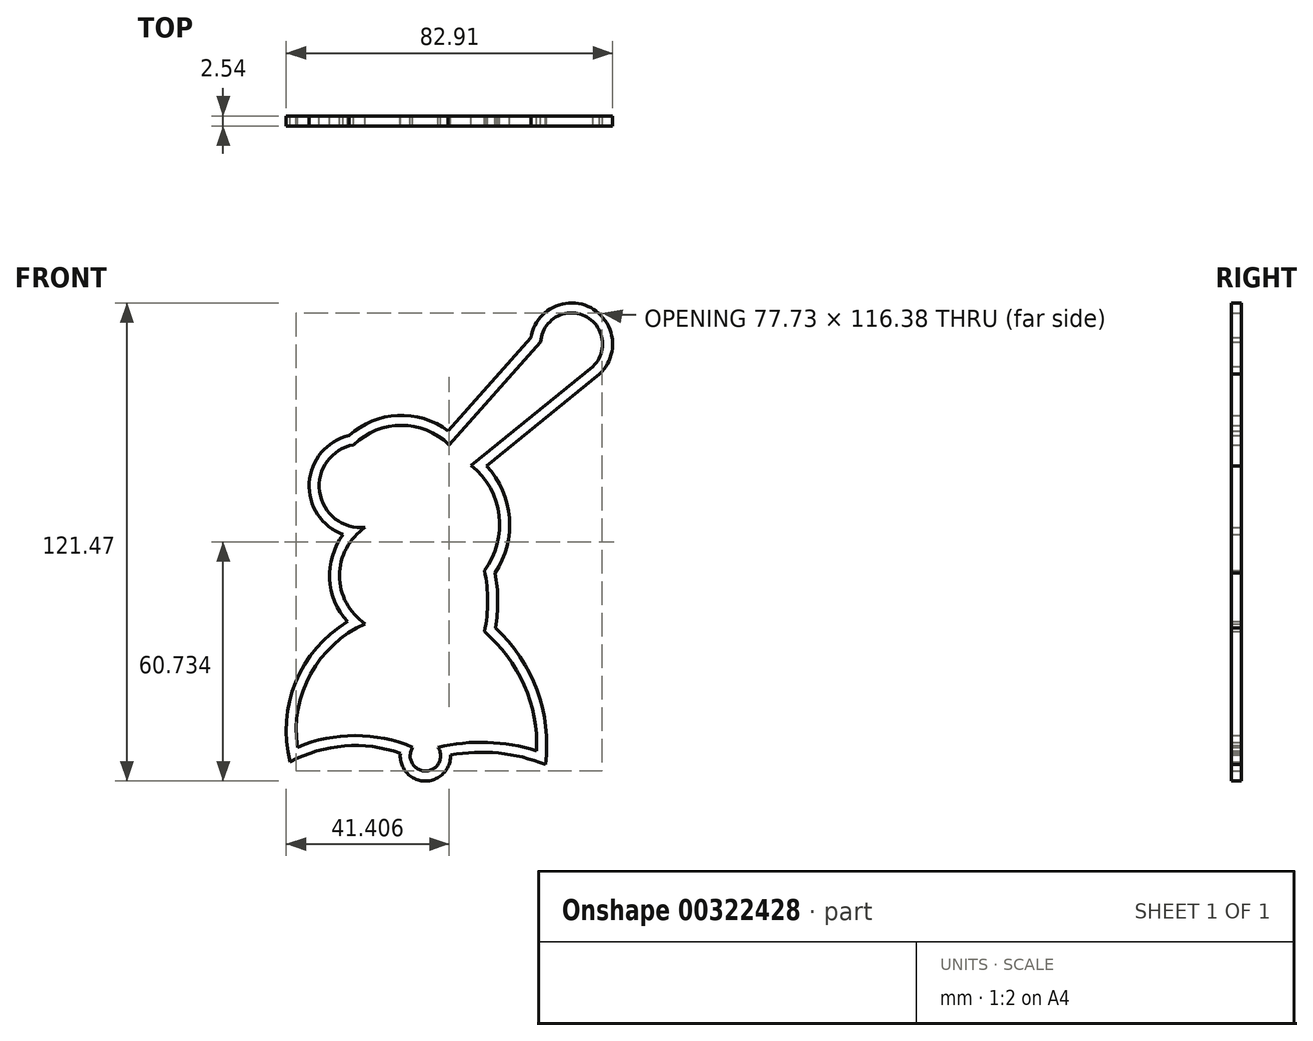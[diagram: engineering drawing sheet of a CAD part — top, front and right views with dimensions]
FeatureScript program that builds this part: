
annotation { "Feature Type Name" : "Feature", "Feature Type Description" : "" }
export const myFeature = defineFeature(function(context is Context, id is Id, definition is map)
    precondition{}
    {
        {
            var Q0;
            Q0=qCreatedBy(makeId("Front.planeOp"),FACE);
            var sketch = newSketch(context, id + "F0", { "sketchPlane" : qUnion([Q0])});
            skArc(sketch, "E0", {"start": v(-24.2, 20.99) * mm, "mid": v(-32.89, 9.08) * mm, "end": v(-21.28, 0) * mm});
            skArc(sketch, "E1", {"start": v(0, 20.99) * mm, "mid": v(-12.1, 25.92) * mm, "end": v(-24.2, 20.99) * mm});
            skLineSegment(sketch, "E2", {"start": v(0, 20.99) * mm, "end": v(23.26, 47.14) * mm});
            skArc(sketch, "E3", {"start": v(36.56, 40.88) * mm, "mid": v(34.49, 53.74) * mm, "end": v(23.26, 47.14) * mm});
            skLineSegment(sketch, "E4", {"start": v(36.56, 40.88) * mm, "end": v(5.63, 15.71) * mm});
            skArc(sketch, "E5", {"start": v(8.96, -10.98) * mm, "mid": v(12.74, 3.04) * mm, "end": v(5.63, 15.71) * mm});
            skArc(sketch, "E6", {"start": v(-21.28, 0) * mm, "mid": v(-27.83, -12.23) * mm, "end": v(-21.28, -24.46) * mm});
            skArc(sketch, "E7", {"start": v(8.96, -26.48) * mm, "mid": v(9.85, -18.73) * mm, "end": v(8.96, -10.98) * mm});
            skArc(sketch, "E8", {"start": v(-21.28, -24.46) * mm, "mid": v(-35.17, -37.27) * mm, "end": v(-38.48, -55.87) * mm});
            skArc(sketch, "E9", {"start": v(22.24, -56.74) * mm, "mid": v(19.11, -40.07) * mm, "end": v(8.96, -26.48) * mm});
            skArc(sketch, "E10", {"start": v(-9.2, -55.87) * mm, "mid": v(-23.85, -52.87) * mm, "end": v(-38.48, -55.87) * mm});
            skArc(sketch, "E11", {"start": v(-9.2, -55.87) * mm, "mid": v(-6, -61.9) * mm, "end": v(-2.8, -55.87) * mm});
            skArc(sketch, "E12", {"start": v(22.24, -56.74) * mm, "mid": v(9.78, -54.61) * mm, "end": v(-2.8, -55.87) * mm});
            skCircle(sketch, "E13", {"center": v(32.03, -52.7) * mm, "radius": 9.82 * mm});
            skSolve(sketch);
        }
        {
            var Q0;
            Q0 = qSketchRegion(id + "F0", true);
            extrude(context, id + "F1", {"entities" : qUnion([Q0]), "depth" : 5 * mm});
        }
        {
            var Q0;
            Q0=makeQuery(id+"F1.opExtrude","SWEPT_BODY",BODY,{"disambiguationData":[OSD([sQuery(id+"F0.wireOp",EDGE,"E13")])]});
            deleteBodies(context, id + "F2", {"entities" : qUnion([Q0])});
        }
        {
            var Q0;
            Q0=makeQuery(id+"F1.opExtrude","CAP_FACE",FACE,{"disambiguationData":[OSD([sQuery(id+"F0.wireOp",EDGE,"E0"),sQuery(id+"F0.wireOp",EDGE,"E1"),sQuery(id+"F0.wireOp",EDGE,"E2"),sQuery(id+"F0.wireOp",EDGE,"E3"),sQuery(id+"F0.wireOp",EDGE,"E4"),sQuery(id+"F0.wireOp",EDGE,"E5"),sQuery(id+"F0.wireOp",EDGE,"E6"),sQuery(id+"F0.wireOp",EDGE,"E7"),sQuery(id+"F0.wireOp",EDGE,"E8"),sQuery(id+"F0.wireOp",EDGE,"E9"),sQuery(id+"F0.wireOp",EDGE,"E10"),sQuery(id+"F0.wireOp",EDGE,"E11"),sQuery(id+"F0.wireOp",EDGE,"E12")])],"isStart":false});
            var sketch = newSketch(context, id + "F3", { "sketchPlane" : qUnion([Q0])});
            skArc(sketch, "E14.0", {"start": v(-12.37, -57.37) * mm, "mid": v(-6.22, -64.43) * mm, "end": v(0.4, -57.8) * mm});
            skArc(sketch, "E14.1", {"start": v(-40.32, -59.57) * mm, "mid": v(-26.58, -55.52) * mm, "end": v(-12.37, -57.37) * mm});
            skLineSegment(sketch, "E14.2", {"start": v(9.5, 15.6) * mm, "end": v(38.23, 38.97) * mm});
            skArc(sketch, "E14.3", {"start": v(11.68, -11.55) * mm, "mid": v(15.36, 2.4) * mm, "end": v(9.5, 15.6) * mm});
            skArc(sketch, "E14.4", {"start": v(11.75, -25.55) * mm, "mid": v(12.39, -18.55) * mm, "end": v(11.68, -11.55) * mm});
            skArc(sketch, "E14.5", {"start": v(24.5, -60.22) * mm, "mid": v(22.36, -41.33) * mm, "end": v(11.75, -25.55) * mm});
            skArc(sketch, "E14.6", {"start": v(38.23, 38.97) * mm, "mid": v(36.03, 55.81) * mm, "end": v(20.83, 48.23) * mm});
            skLineSegment(sketch, "E14.7", {"start": v(20.83, 48.23) * mm, "end": v(-0.25, 24.53) * mm});
            skArc(sketch, "E14.8", {"start": v(0.4, -57.8) * mm, "mid": v(12.61, -57.35) * mm, "end": v(24.5, -60.22) * mm});
            skArc(sketch, "E14.9", {"start": v(-0.25, 24.53) * mm, "mid": v(-13.04, 28.44) * mm, "end": v(-25.41, 23.33) * mm});
            skArc(sketch, "E14.10", {"start": v(-25.41, 23.33) * mm, "mid": v(-35.5, 11.3) * mm, "end": v(-26.87, -1.81) * mm});
            skArc(sketch, "E14.11", {"start": v(-26.87, -1.81) * mm, "mid": v(-30.35, -13.08) * mm, "end": v(-25.78, -23.95) * mm});
            skArc(sketch, "E14.12", {"start": v(-25.78, -23.95) * mm, "mid": v(-38.97, -39.35) * mm, "end": v(-40.32, -59.57) * mm});
            skArc(sketch, "E15.0", {"start": v(-9.2, -55.87) * mm, "mid": v(-6, -61.9) * mm, "end": v(-2.8, -55.87) * mm});
            skArc(sketch, "E15.1", {"start": v(-38.48, -55.87) * mm, "mid": v(-23.85, -52.87) * mm, "end": v(-9.2, -55.87) * mm});
            skLineSegment(sketch, "E15.2", {"start": v(5.63, 15.71) * mm, "end": v(36.56, 40.88) * mm});
            skArc(sketch, "E15.3", {"start": v(8.96, -10.98) * mm, "mid": v(12.74, 3.04) * mm, "end": v(5.63, 15.71) * mm});
            skArc(sketch, "E15.4", {"start": v(8.96, -26.48) * mm, "mid": v(9.85, -18.73) * mm, "end": v(8.96, -10.98) * mm});
            skArc(sketch, "E15.5", {"start": v(22.24, -56.74) * mm, "mid": v(19.11, -40.07) * mm, "end": v(8.96, -26.48) * mm});
            skArc(sketch, "E15.6", {"start": v(36.56, 40.88) * mm, "mid": v(34.49, 53.74) * mm, "end": v(23.26, 47.14) * mm});
            skLineSegment(sketch, "E15.7", {"start": v(23.26, 47.14) * mm, "end": v(0, 20.99) * mm});
            skArc(sketch, "E15.8", {"start": v(-2.8, -55.87) * mm, "mid": v(9.78, -54.61) * mm, "end": v(22.24, -56.74) * mm});
            skArc(sketch, "E15.9", {"start": v(0, 20.99) * mm, "mid": v(-12.1, 25.92) * mm, "end": v(-24.2, 20.99) * mm});
            skArc(sketch, "E15.10", {"start": v(-24.2, 20.99) * mm, "mid": v(-32.89, 9.08) * mm, "end": v(-21.28, 0) * mm});
            skArc(sketch, "E15.11", {"start": v(-21.28, 0) * mm, "mid": v(-27.83, -12.23) * mm, "end": v(-21.28, -24.46) * mm});
            skArc(sketch, "E15.12", {"start": v(-21.28, -24.46) * mm, "mid": v(-35.17, -37.27) * mm, "end": v(-38.48, -55.87) * mm});
            skSolve(sketch);
        }
        {
            var Q0;
            Q0=makeQuery(id+"F3.imprint","IMPRINT",FACE,{"disambiguationData":[TD([[makeQuery(id+"F3.imprint","IMPRINT",EDGE,{"derivedFrom":sQuery(id+"F3.wireOp",EDGE,"E14.0")}),1.0]])]});
            extrude(context, id + "F4", {"entities" : qUnion([Q0]), "depth" : 2.54 * mm});
        }
        {
            var Q0;
            Q0=makeQuery(id+"F1.opExtrude","CAP_FACE",FACE,{"disambiguationData":[OSD([sQuery(id+"F0.wireOp",EDGE,"E0"),sQuery(id+"F0.wireOp",EDGE,"E1"),sQuery(id+"F0.wireOp",EDGE,"E2"),sQuery(id+"F0.wireOp",EDGE,"E3"),sQuery(id+"F0.wireOp",EDGE,"E4"),sQuery(id+"F0.wireOp",EDGE,"E5"),sQuery(id+"F0.wireOp",EDGE,"E6"),sQuery(id+"F0.wireOp",EDGE,"E7"),sQuery(id+"F0.wireOp",EDGE,"E8"),sQuery(id+"F0.wireOp",EDGE,"E9"),sQuery(id+"F0.wireOp",EDGE,"E10"),sQuery(id+"F0.wireOp",EDGE,"E11"),sQuery(id+"F0.wireOp",EDGE,"E12")])],"isStart":false});
            extrude(context, id + "F5", {"entities" : qUnion([Q0]), "operationType" : NewBodyOperationType.REMOVE, "oppositeDirection" : true, "depth" : 25.4 * mm});
        }
        {
            var Q0;
            Q0=makeQuery(id+"F4.opExtrude","CAP_FACE",FACE,{"disambiguationData":[OSD([sQuery(id+"F3.wireOp",EDGE,"E14.0"),sQuery(id+"F3.wireOp",EDGE,"E14.1"),sQuery(id+"F3.wireOp",EDGE,"E14.2"),sQuery(id+"F3.wireOp",EDGE,"E14.3"),sQuery(id+"F3.wireOp",EDGE,"E14.4"),sQuery(id+"F3.wireOp",EDGE,"E14.5"),sQuery(id+"F3.wireOp",EDGE,"E14.6"),sQuery(id+"F3.wireOp",EDGE,"E14.7"),sQuery(id+"F3.wireOp",EDGE,"E14.8"),sQuery(id+"F3.wireOp",EDGE,"E14.9"),sQuery(id+"F3.wireOp",EDGE,"E14.10"),sQuery(id+"F3.wireOp",EDGE,"E14.11"),sQuery(id+"F3.wireOp",EDGE,"E14.12"),sQuery(id+"F3.wireOp",EDGE,"E15.0"),sQuery(id+"F3.wireOp",EDGE,"E15.1"),sQuery(id+"F3.wireOp",EDGE,"E15.2"),sQuery(id+"F3.wireOp",EDGE,"E15.3"),sQuery(id+"F3.wireOp",EDGE,"E15.4"),sQuery(id+"F3.wireOp",EDGE,"E15.5"),sQuery(id+"F3.wireOp",EDGE,"E15.6"),sQuery(id+"F3.wireOp",EDGE,"E15.7"),sQuery(id+"F3.wireOp",EDGE,"E15.8"),sQuery(id+"F3.wireOp",EDGE,"E15.9"),sQuery(id+"F3.wireOp",EDGE,"E15.10"),sQuery(id+"F3.wireOp",EDGE,"E15.11"),sQuery(id+"F3.wireOp",EDGE,"E15.12")])],"isStart":false});
            var sketch = newSketch(context, id + "F6", { "sketchPlane" : qUnion([Q0])});
            skCircle(sketch, "E16", {"center": v(33.1, -48.06) * mm, "radius": 8.8 * mm});
            skSolve(sketch);
        }
    });
